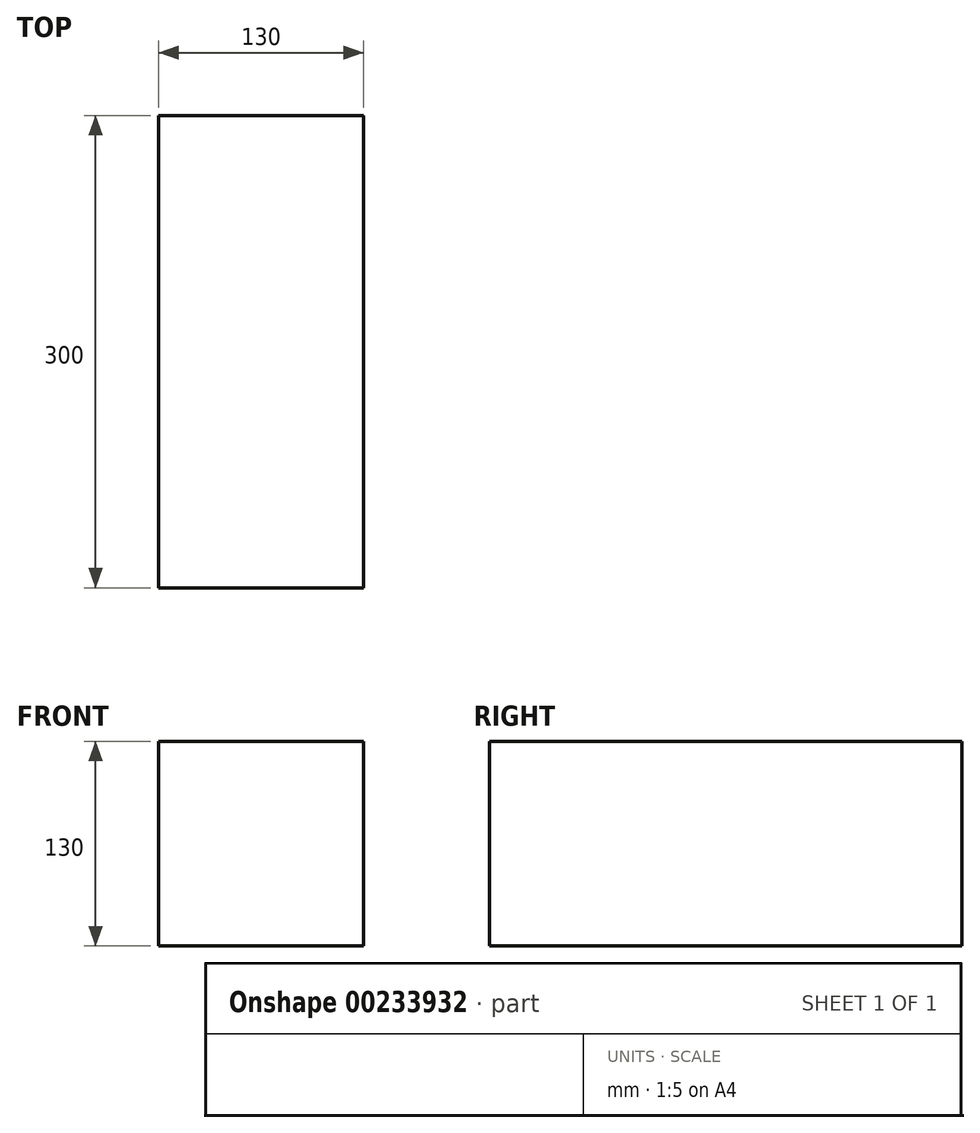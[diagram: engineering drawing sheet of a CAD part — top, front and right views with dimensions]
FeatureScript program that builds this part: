
annotation { "Feature Type Name" : "Feature", "Feature Type Description" : "" }
export const myFeature = defineFeature(function(context is Context, id is Id, definition is map)
    precondition{}
    {
        {
            var Q0;
            Q0=qCreatedBy(makeId("Front.planeOp"),FACE);
            var sketch = newSketch(context, id + "F0", { "sketchPlane" : qUnion([Q0])});
            skLineSegment(sketch, "E0.bottom", {"start": v(-152.13, 151.48) * mm, "end": v(-22.13, 151.48) * mm});
            skLineSegment(sketch, "E0.top", {"start": v(-152.13, 21.48) * mm, "end": v(-22.13, 21.48) * mm});
            skLineSegment(sketch, "E0.left", {"start": v(-152.13, 151.48) * mm, "end": v(-152.13, 21.48) * mm});
            skLineSegment(sketch, "E0.right", {"start": v(-22.13, 151.48) * mm, "end": v(-22.13, 21.48) * mm});
            skSolve(sketch);
        }
        {
            var Q0;
            Q0=makeQuery(id+"F0.imprint","IMPRINT",FACE,{"disambiguationData":[TD([[makeQuery(id+"F0.imprint","IMPRINT",EDGE,{"derivedFrom":sQuery(id+"F0.wireOp",EDGE,"E0.bottom")}),-1.0]])]});
            extrude(context, id + "F1", {"entities" : qUnion([Q0]), "depth" : 300 * mm});
        }
    });
